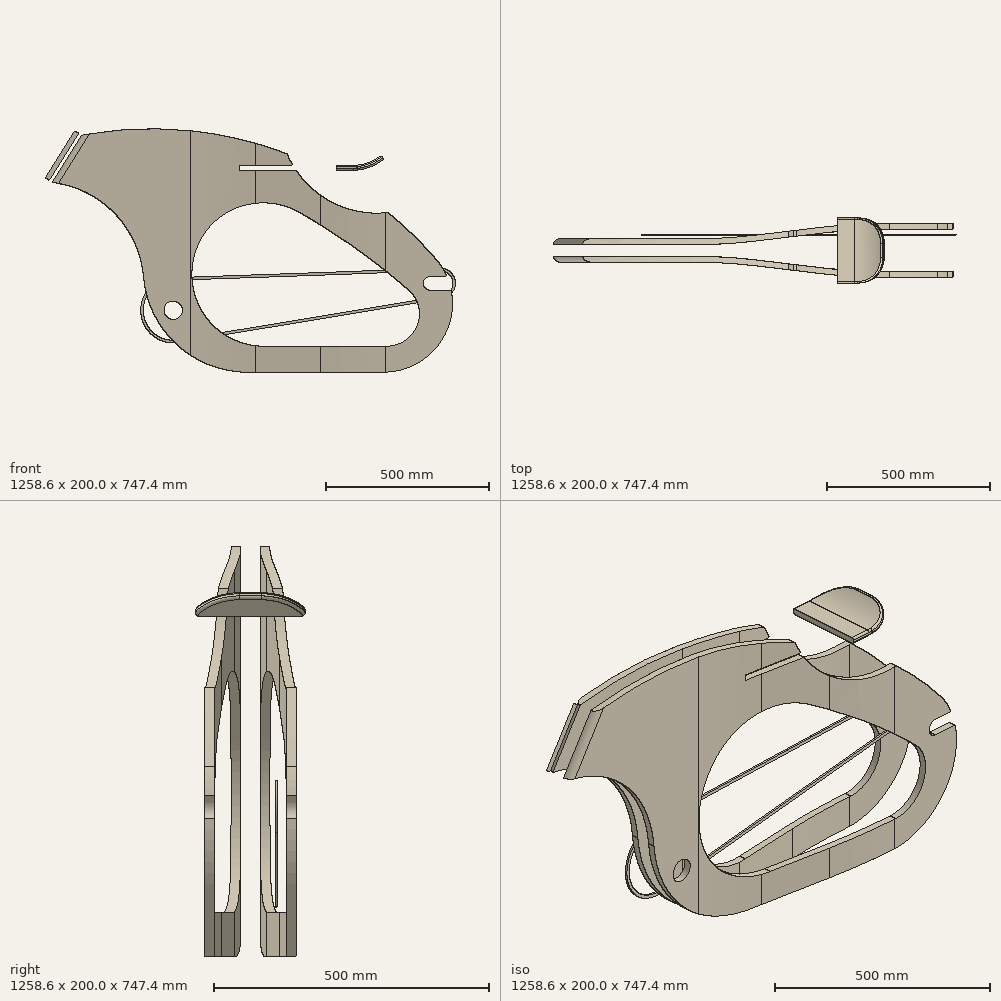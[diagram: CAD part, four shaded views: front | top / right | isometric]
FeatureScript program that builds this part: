
annotation { "Feature Type Name" : "Feature", "Feature Type Description" : "" }
export const myFeature = defineFeature(function(context is Context, id is Id, definition is map)
    precondition{}
    {
        {
            var Q0;
            Q0=qCreatedBy(makeId("Front.planeOp"),FACE);
            var sketch = newSketch(context, id + "F0", { "sketchPlane" : qUnion([Q0])});
            skCircle(sketch, "E0", {"center": v(766, 332.5) * mm, "radius": 332.5 * mm});
            skCircle(sketch, "E1", {"center": v(766, 332.5) * mm, "radius": 287.5 * mm});
            skLineSegment(sketch, "E2", {"start": v(-655.9, 304.94) * mm, "end": v(-438.79, 652.4) * mm});
            skCircle(sketch, "E3.0", {"center": v(766, 332.5) * mm, "radius": 269.5 * mm});
            skLineSegment(sketch, "E4", {"start": v(-438.79, 652.4) * mm, "end": v(-348.7, 796.57) * mm});
            skLineSegment(sketch, "E5", {"start": v(-700, 332.5) * mm, "end": v(-655.9, 304.94) * mm});
            skLineSegment(sketch, "E6.rect.bottom", {"start": v(-423.52, 642.86) * mm, "end": v(-454.05, 661.94) * mm});
            skLineSegment(sketch, "E6.rect.top", {"start": v(-333.44, 787.03) * mm, "end": v(-363.97, 806.1) * mm});
            skLineSegment(sketch, "E6.rect.right", {"start": v(-454.05, 661.94) * mm, "end": v(-363.97, 806.1) * mm});
            skPoint(sketch, "E6.rect.middle", {"position": v(-393.74, 724.48) * mm});
            skLineSegment(sketch, "E7", {"start": v(-333.44, 787.03) * mm, "end": v(-423.52, 642.86) * mm});
            skCircle(sketch, "E8", {"center": v(766, 332.5) * mm, "radius": 6 * mm, "construction": true});
            skLineSegment(sketch, "E9", {"start": v(736, 338.5) * mm, "end": v(796, 338.5) * mm, "construction": true});
            skLineSegment(sketch, "E10", {"start": v(736, 326.5) * mm, "end": v(796, 326.5) * mm, "construction": true});
            skArc(sketch, "E11", {"start": v(736, 338.5) * mm, "mid": v(730, 332.5) * mm, "end": v(736, 326.5) * mm, "construction": true});
            skLineSegment(sketch, "E12.bottom", {"start": v(796, 358.5) * mm, "end": v(711, 358.5) * mm, "construction": true});
            skLineSegment(sketch, "E12.top", {"start": v(796, 306.5) * mm, "end": v(711, 306.5) * mm, "construction": true});
            skLineSegment(sketch, "E12.left", {"start": v(796, 358.5) * mm, "end": v(796, 338.5) * mm, "construction": true});
            skLineSegment(sketch, "E12.right", {"start": v(711, 358.5) * mm, "end": v(711, 306.5) * mm, "construction": true});
            skLineSegment(sketch, "E13.trimOffspring", {"start": v(796, 326.5) * mm, "end": v(796, 306.5) * mm, "construction": true});
            skCircle(sketch, "E14", {"center": v(-700, 332.5) * mm, "radius": 332.5 * mm});
            skSolve(sketch);
        }
        {
            var Q0;
            Q0=qCreatedBy(makeId("Front.planeOp"),FACE);
            var sketch = newSketch(context, id + "F1", { "sketchPlane" : qUnion([Q0])});
            skCircle(sketch, "E15", {"center": v(-52.74, 250) * mm, "radius": 28 * mm});
            skPoint(sketch, "E16.rect.middle", {"position": v(-393.74, 724.48) * mm});
            skCircle(sketch, "E17", {"center": v(-52.74, 250) * mm, "radius": 220 * mm, "construction": true});
            skLineSegment(sketch, "E18", {"start": v(-333.44, 787.03) * mm, "end": v(-423.52, 642.86) * mm});
            skCircle(sketch, "E19", {"center": v(766.48, 332.5) * mm, "radius": 6 * mm, "construction": true});
            skArc(sketch, "E20", {"start": v(499.62, 680) * mm, "mid": v(549.62, 688.58) * mm, "end": v(593.9, 713.33) * mm});
            skLineSegment(sketch, "E21", {"start": v(499.62, 680) * mm, "end": v(149.62, 680) * mm});
            skArc(sketch, "E22", {"start": v(-144.1, 352.65) * mm, "mid": v(-41.65, 144.25) * mm, "end": v(174.74, 60) * mm});
            skArc(sketch, "E23", {"start": v(-144.1, 352.65) * mm, "mid": v(-232.4, 547.25) * mm, "end": v(-423.52, 642.86) * mm});
            skArc(sketch, "E24", {"start": v(786.48, 60) * mm, "mid": v(881.52, 114.61) * mm, "end": v(882.18, 224.23) * mm, "construction": true});
            skLineSegment(sketch, "E25", {"start": v(174.74, 60) * mm, "end": v(786.48, 60) * mm});
            skLineSegment(sketch, "E26", {"start": v(896.48, 395.04) * mm, "end": v(896.48, -82) * mm, "construction": true});
            skLineSegment(sketch, "E27", {"start": v(858.4, 311.5) * mm, "end": v(736, 311.5) * mm});
            skArc(sketch, "E28", {"start": v(736, 311.5) * mm, "mid": v(715, 332.5) * mm, "end": v(736, 353.5) * mm});
            skLineSegment(sketch, "E29", {"start": v(736, 353.5) * mm, "end": v(830.06, 353.5) * mm});
            skArc(sketch, "E30", {"start": v(296.56, 729.92) * mm, "mid": v(421.78, 588.55) * mm, "end": v(606.66, 550) * mm});
            skArc(sketch, "E31.trimOffspring", {"start": v(296.56, 729.92) * mm, "mid": v(-14.43, 802.69) * mm, "end": v(-333.44, 787.03) * mm});
            skArc(sketch, "E32", {"start": v(882.18, 224.23) * mm, "mid": v(633.17, 527.8) * mm, "end": v(296.56, 729.92) * mm, "construction": true});
            skArc(sketch, "E33", {"start": v(882.18, 224.23) * mm, "mid": v(759.66, 400) * mm, "end": v(606.66, 550) * mm});
            skArc(sketch, "E34", {"start": v(594.53, 60) * mm, "mid": v(785.37, 182.37) * mm, "end": v(753.8, 406.86) * mm});
            skSolve(sketch);
        }
        {
            var Q0;
            Q0=qCreatedBy(makeId("Front.planeOp"),FACE);
            var sketch = newSketch(context, id + "F2", { "sketchPlane" : qUnion([Q0])});
            skArc(sketch, "E35.4", {"start": v(332.47, 551.53) * mm, "mid": v(11.46, 415.97) * mm, "end": v(224.22, 140) * mm});
            skLineSegment(sketch, "E35.5", {"start": v(224.22, 140) * mm, "end": v(726.48, 140) * mm});
            skArc(sketch, "E36", {"start": v(726.48, 140) * mm, "mid": v(772.68, 170.88) * mm, "end": v(761.81, 225.37) * mm, "construction": true});
            skArc(sketch, "E37", {"start": v(761.81, 225.37) * mm, "mid": v(558.18, 402.98) * mm, "end": v(332.47, 551.53) * mm});
            skLineSegment(sketch, "E38", {"start": v(827.43, 311.5) * mm, "end": v(736, 311.5) * mm});
            skLineSegment(sketch, "E39", {"start": v(736, 353.5) * mm, "end": v(796.96, 353.5) * mm});
            skArc(sketch, "E40", {"start": v(736, 311.5) * mm, "mid": v(715, 332.5) * mm, "end": v(736, 353.5) * mm});
            skArc(sketch, "E41", {"start": v(796.96, 353.5) * mm, "mid": v(822.9, 340.27) * mm, "end": v(827.43, 311.5) * mm});
            skArc(sketch, "E42", {"start": v(604.53, 140) * mm, "mid": v(696.45, 203.56) * mm, "end": v(669.42, 312) * mm});
            skSolve(sketch);
        }
        {
            var Q0;
            Q0=sQuery(id+"F0.wireOp",VERTEX,"E2.end");
            var Q1;
            Q1=sQuery(id+"F0.wireOp",EDGE,"E2");
            cPlane(context, id + "F3", {"entities" : qUnion([Q0, Q1]), "cplaneType" : CPlaneType.CURVE_POINT, "offset" : 150 * mm, "width" : 150 * mm, "height" : 150 * mm});
        }
        {
            var Q0;
            Q0=qCreatedBy(id+"F3.planeOp",FACE);
            var sketch = newSketch(context, id + "F4", { "sketchPlane" : qUnion([Q0])});
            skCircle(sketch, "E43", {"center": v(-717.83, 0) * mm, "radius": 19 * mm});
            skSolve(sketch);
        }
        {
            var Q0;
            Q0=makeQuery(id+"F4.imprint","IMPRINT",FACE,{"disambiguationData":[TD([[makeQuery(id+"F4.imprint","IMPRINT",EDGE,{"derivedFrom":sQuery(id+"F4.wireOp",EDGE,"E43")}),1.0]])]});
            extrude(context, id + "F5", {"entities" : qUnion([Q0]), "depth" : 170 * mm});
        }
        {
            var Q0;
            Q0=makeQuery(id+"F5.opExtrude","CAP_FACE",FACE,{"disambiguationData":[OSD([sQuery(id+"F4.wireOp",EDGE,"E43")])],"isStart":false});
            var Q1;
            Q1=makeQuery(id+"F5.opExtrude","CAP_FACE",FACE,{"disambiguationData":[OSD([sQuery(id+"F4.wireOp",EDGE,"E43")])],"isStart":true});
            shell(context, id + "F6", {"entities" : qUnion([Q0, Q1]), "thickness" : 2 * mm});
        }
        {
            var Q0;
            Q0=sQuery(id+"F0.wireOp",EDGE,"E2");
            cPlane(context, id + "F7", {"entities" : qUnion([Q0]), "cplaneType" : CPlaneType.LINE_ANGLE, "offset" : 150 * mm, "angle" : 0 * degree, "width" : 150 * mm, "height" : 150 * mm});
        }
        {
            var Q0;
            Q0=qCreatedBy(id+"F7.planeOp",FACE);
            var sketch = newSketch(context, id + "F8", { "sketchPlane" : qUnion([Q0])});
            skLineSegment(sketch, "E44", {"start": v(0, 181.22) * mm, "end": v(0, -136.17) * mm, "construction": true});
            skLineSegment(sketch, "E45", {"start": v(-70, -99.25) * mm, "end": v(-70, 210.75) * mm});
            skArc(sketch, "E46", {"start": v(-70, 210.75) * mm, "mid": v(0, 280.75) * mm, "end": v(70, 210.75) * mm});
            skLineSegment(sketch, "E47", {"start": v(70, 210.75) * mm, "end": v(70, -99.25) * mm});
            skLineSegment(sketch, "E48", {"start": v(0, 280.75) * mm, "end": v(0, 606.14) * mm});
            skSolve(sketch);
        }
        {
            var Q0;
            Q0=sQuery(id+"F8.wireOp",VERTEX,"E45.start");
            var Q1;
            Q1=sQuery(id+"F8.wireOp",EDGE,"E45");
            cPlane(context, id + "F9", {"entities" : qUnion([Q0, Q1]), "cplaneType" : CPlaneType.CURVE_POINT, "offset" : 150 * mm, "width" : 150 * mm, "height" : 150 * mm});
        }
        {
            var Q0;
            Q0=qCreatedBy(id+"F9.planeOp",FACE);
            var sketch = newSketch(context, id + "F10", { "sketchPlane" : qUnion([Q0])});
            skCircle(sketch, "E49", {"center": v(-717.83, -70) * mm, "radius": 14.29 * mm});
            skSolve(sketch);
        }
        {
            var Q0;
            Q0=makeQuery(id+"F10.imprint","IMPRINT",FACE,{"disambiguationData":[TD([[makeQuery(id+"F10.imprint","IMPRINT",EDGE,{"derivedFrom":sQuery(id+"F10.wireOp",EDGE,"E49")}),1.0]])]});
            var Q1;
            Q1=sQuery(id+"F10.wireOp",EDGE,"E49");
            var Q2;
            Q2=sQuery(id+"F8.wireOp",EDGE,"E45");
            var Q3;
            Q3=sQuery(id+"F8.wireOp",EDGE,"E46");
            var Q4;
            Q4=sQuery(id+"F8.wireOp",EDGE,"E47");
            sweep(context, id + "F11", {"profiles" : qUnion([Q0]), "surfaceProfiles" : qUnion([Q1]), "path" : qUnion([Q2, Q3, Q4])});
        }
        {
            var Q0;
            Q0=sQuery(id+"F8.wireOp",EDGE,"E48");
            var Q1;
            Q1=sQuery(id+"F8.wireOp",VERTEX,"E48.start");
            cPlane(context, id + "F12", {"entities" : qUnion([Q0, Q1]), "cplaneType" : CPlaneType.CURVE_POINT, "offset" : 150 * mm, "width" : 150 * mm, "height" : 150 * mm});
        }
        {
            var Q0;
            Q0=qCreatedBy(id+"F12.planeOp",FACE);
            var sketch = newSketch(context, id + "F13", { "sketchPlane" : qUnion([Q0])});
            skCircle(sketch, "E50", {"center": v(-717.83, 0) * mm, "radius": 14.29 * mm});
            skSolve(sketch);
        }
        {
            var Q0;
            Q0=makeQuery(id+"F13.imprint","IMPRINT",FACE,{"disambiguationData":[TD([[makeQuery(id+"F13.imprint","IMPRINT",EDGE,{"derivedFrom":sQuery(id+"F13.wireOp",EDGE,"E50")}),1.0]])]});
            extrude(context, id + "F14", {"entities" : qUnion([Q0]), "operationType" : NewBodyOperationType.ADD, "depth" : 250 * mm});
        }
        {
            var Q0;
            Q0=makeQuery(id+"F11.opSweep","CAP_FACE",FACE,{"disambiguationData":[OSD([sQuery(id+"F8.wireOp",VERTEX,"E45.start"),sQuery(id+"F10.wireOp",EDGE,"E49")])],"isStart":true});
            var Q1;
            Q1=makeQuery(id+"F11.opSweep","CAP_FACE",FACE,{"disambiguationData":[OSD([sQuery(id+"F8.wireOp",VERTEX,"E47.end"),sQuery(id+"F10.wireOp",EDGE,"E49")])],"isStart":false});
            var Q2;
            Q2=makeQuery(id+"F14.opExtrude","CAP_FACE",FACE,{"disambiguationData":[OSD([sQuery(id+"F13.wireOp",EDGE,"E50")])],"isStart":false});
            shell(context, id + "F15", {"entities" : qUnion([Q0, Q1, Q2]), "thickness" : 2 * mm});
        }
        {
            var Q0;
            Q0=qCreatedBy(makeId("Top.planeOp"),FACE);
            var sketch = newSketch(context, id + "F16", { "sketchPlane" : qUnion([Q0])});
            skLineSegment(sketch, "E51", {"start": v(1100, 65) * mm, "end": v(600, 65) * mm});
            skLineSegment(sketch, "E52", {"start": v(-998.59, 17.5) * mm, "end": v(1.41, 17.5) * mm});
            skArc(sketch, "E53", {"start": v(1.41, 17.5) * mm, "mid": v(101.59, 20.48) * mm, "end": v(201.41, 29.4) * mm});
            skArc(sketch, "E54", {"start": v(600, 65) * mm, "mid": v(499.82, 62.02) * mm, "end": v(400, 53.1) * mm});
            skLineSegment(sketch, "E55", {"start": v(201.41, 29.4) * mm, "end": v(400, 53.1) * mm});
            skLineSegment(sketch, "E56.0", {"start": v(1100, 83) * mm, "end": v(600, 83) * mm});
            skArc(sketch, "E56.1", {"start": v(600, 83) * mm, "mid": v(498.75, 80) * mm, "end": v(397.87, 70.98) * mm});
            skLineSegment(sketch, "E56.2", {"start": v(199.28, 47.27) * mm, "end": v(397.87, 70.98) * mm});
            skArc(sketch, "E56.3", {"start": v(1.41, 35.5) * mm, "mid": v(100.52, 38.44) * mm, "end": v(199.28, 47.27) * mm});
            skLineSegment(sketch, "E56.4", {"start": v(-998.59, 35.5) * mm, "end": v(1.41, 35.5) * mm});
            skLineSegment(sketch, "E57", {"start": v(1100, 65) * mm, "end": v(1100, 83) * mm});
            skLineSegment(sketch, "E58", {"start": v(-998.59, 17.5) * mm, "end": v(-998.59, 35.5) * mm});
            skSolve(sketch);
        }
        {
            var Q0;
            Q0=makeQuery(id+"F1.imprint","IMPRINT",FACE,{"disambiguationData":[TD([[makeQuery(id+"F1.imprint","IMPRINT",EDGE,{"derivedFrom":sQuery(id+"F1.wireOp",EDGE,"E15")}),-1.0]])]});
            extrude(context, id + "F17", {"entities" : qUnion([Q0]), "oppositeDirection" : true, "depth" : 150 * mm});
        }
        {
            var Q0;
            Q0=makeQuery(id+"F2.imprint","IMPRINT",FACE,{"disambiguationData":[TD([[makeQuery(id+"F2.imprint","IMPRINT",EDGE,{"derivedFrom":sQuery(id+"F2.wireOp",EDGE,"E35.4")}),1.0]])]});
            var Q1;
            Q1=makeQuery(id+"F2.imprint","IMPRINT",FACE,{"disambiguationData":[TD([[makeQuery(id+"F2.imprint","IMPRINT",EDGE,{"derivedFrom":sQuery(id+"F2.wireOp",EDGE,"E38")}),-1.0]])]});
            extrude(context, id + "F18", {"entities" : qUnion([Q0, Q1]), "operationType" : NewBodyOperationType.REMOVE, "oppositeDirection" : true, "depth" : 200 * mm});
        }
        {
            var Q0;
            Q0=qCreatedBy(makeId("Front.planeOp"),FACE);
            var sketch = newSketch(context, id + "F19", { "sketchPlane" : qUnion([Q0])});
            skLineSegment(sketch, "E59", {"start": v(499.62, 680) * mm, "end": v(149.62, 680) * mm});
            skArc(sketch, "E60", {"start": v(499.62, 680) * mm, "mid": v(549.62, 688.58) * mm, "end": v(593.9, 713.33) * mm});
            skArc(sketch, "E61.0", {"start": v(499.62, 695) * mm, "mid": v(544.62, 702.72) * mm, "end": v(584.47, 725) * mm});
            skLineSegment(sketch, "E61.1", {"start": v(499.62, 695) * mm, "end": v(149.62, 695) * mm});
            skLineSegment(sketch, "E62", {"start": v(593.9, 713.33) * mm, "end": v(584.47, 725) * mm});
            skLineSegment(sketch, "E63", {"start": v(149.62, 680) * mm, "end": v(149.62, 695) * mm});
            skSolve(sketch);
        }
        {
            var Q0;
            Q0=makeQuery(id+"F16.imprint","IMPRINT",FACE,{"disambiguationData":[TD([[makeQuery(id+"F16.imprint","IMPRINT",EDGE,{"derivedFrom":sQuery(id+"F16.wireOp",EDGE,"E51")}),-1.0]])]});
            extrude(context, id + "F20", {"entities" : qUnion([Q0]), "operationType" : NewBodyOperationType.INTERSECT, "depth" : 1000 * mm});
        }
        {
            var Q0;
            Q0=makeQuery(id+"F17.opExtrude","SWEPT_BODY",BODY,{"disambiguationData":[OSD([sQuery(id+"F1.wireOp",EDGE,"E15"),sQuery(id+"F1.wireOp",EDGE,"E18"),sQuery(id+"F1.wireOp",EDGE,"f25a1a5c-b35a-4eaa-8e16-6169ae110cd0"),sQuery(id+"F1.wireOp",EDGE,"56185d79-83a2-4922-81b8-f2a27202fd78"),sQuery(id+"F1.wireOp",EDGE,"c2120ab2-a2c6-4db6-bdfa-dd0143dbe7f6"),sQuery(id+"F1.wireOp",EDGE,"d6b472ae-8588-43ed-990c-50ee3ed74349"),sQuery(id+"F1.wireOp",EDGE,"64d2bcdb-48c4-4ea9-94b1-3d4cdc629e19"),sQuery(id+"F1.wireOp",EDGE,"7d159a81-d20a-4d29-8569-c734789b89ba.0"),sQuery(id+"F1.wireOp",EDGE,"7d159a81-d20a-4d29-8569-c734789b89ba.1"),sQuery(id+"F1.wireOp",EDGE,"7d159a81-d20a-4d29-8569-c734789b89ba.2"),sQuery(id+"F1.wireOp",EDGE,"fa78dc51-c197-49c6-b8ef-f44956650a6e"),sQuery(id+"F1.wireOp",EDGE,"1d27aa24-91d2-4d14-8a43-1a7035f57801"),sQuery(id+"F1.wireOp",EDGE,"E22"),sQuery(id+"F1.wireOp",EDGE,"b122f575-9e76-4623-8be3-a576d456f2d0"),sQuery(id+"F1.wireOp",EDGE,"E23")])]});
            var Q1;
            Q1=qCreatedBy(makeId("Front.planeOp"),FACE);
            mirror(context, id + "F21", {"entities" : qUnion([Q0]), "mirrorPlane" : qUnion([Q1])});
        }
        {
            var Q0;
            Q0=makeQuery(id+"F19.imprint","IMPRINT",FACE,{"disambiguationData":[TD([[makeQuery(id+"F19.imprint","IMPRINT",EDGE,{"derivedFrom":sQuery(id+"F19.wireOp",EDGE,"E59")}),-1.0]])]});
            extrude(context, id + "F22", {"entities" : qUnion([Q0]), "endBound" : BoundingType.SYMMETRIC, "depth" : 200 * mm});
        }
        {
            var Q0;
            Q0=makeQuery(id+"F22.opExtrude","CAP_EDGE",EDGE,{"disambiguationData":[OSD([sQuery(id+"F19.wireOp",EDGE,"E62")])],"isStart":false});
            var Q1;
            Q1=makeQuery(id+"F22.opExtrude","CAP_EDGE",EDGE,{"disambiguationData":[OSD([sQuery(id+"F19.wireOp",EDGE,"E62")])],"isStart":true});
            fillet(context, id + "F23", {"entities" : qUnion([Q0, Q1]), "radius" : 80 * mm, "tangentPropagation" : true, "allowEdgeOverflow" : false});
        }
        {
            var Q0;
            Q0=makeQuery(id+"F22.opExtrude","CAP_EDGE",EDGE,{"disambiguationData":[OSD([sQuery(id+"F19.wireOp",EDGE,"E63")])],"isStart":false});
            chamfer(context, id + "F24", {"entities" : qUnion([Q0]), "chamferType" : ChamferType.TWO_OFFSETS, "width1" : 30 * mm, "oppositeDirection" : false, "width2" : 200 * mm});
        }
        {
            var Q0;
            Q0=makeQuery(id+"F22.opExtrude","CAP_EDGE",EDGE,{"disambiguationData":[OSD([sQuery(id+"F19.wireOp",EDGE,"E63")])],"isStart":true});
            chamfer(context, id + "F25", {"entities" : qUnion([Q0]), "chamferType" : ChamferType.TWO_OFFSETS, "width1" : 200 * mm, "oppositeDirection" : false, "width2" : 30 * mm, "tangentPropagation" : true});
        }
        {
            var Q0;
            {var subQ0=sQuery(id+"F19.wireOp",EDGE,"E63");Q0=makeQuery(id+"F24.opChamfer","BLEND_EDGE",EDGE,{"blendedFrom":[makeQuery(id+"F22.opExtrude","CAP_EDGE",EDGE,{"disambiguationData":[OSD([subQ0])],"isStart":false}),makeQuery(id+"F22.opExtrude","CAP_FACE",FACE,{"disambiguationData":[OSD([sQuery(id+"F19.wireOp",EDGE,"E59"),sQuery(id+"F19.wireOp",EDGE,"E60"),sQuery(id+"F19.wireOp",EDGE,"E61.0"),sQuery(id+"F19.wireOp",EDGE,"E61.1"),sQuery(id+"F19.wireOp",EDGE,"E62"),subQ0])],"isStart":false})],"blendedInto":[makeQuery(id+"F22.opExtrude","CAP_FACE",FACE,{"disambiguationData":[OSD([sQuery(id+"F19.wireOp",EDGE,"E59"),sQuery(id+"F19.wireOp",EDGE,"E60"),sQuery(id+"F19.wireOp",EDGE,"E61.0"),sQuery(id+"F19.wireOp",EDGE,"E61.1"),sQuery(id+"F19.wireOp",EDGE,"E62"),subQ0])],"isStart":false})]});}
            var Q1;
            {var subQ0=sQuery(id+"F19.wireOp",EDGE,"E63");Q1=makeQuery(id+"F25.opChamfer","BLEND_EDGE",EDGE,{"blendedFrom":[makeQuery(id+"F22.opExtrude","CAP_EDGE",EDGE,{"disambiguationData":[OSD([subQ0])],"isStart":true}),makeQuery(id+"F22.opExtrude","CAP_FACE",FACE,{"disambiguationData":[OSD([sQuery(id+"F19.wireOp",EDGE,"E59"),sQuery(id+"F19.wireOp",EDGE,"E60"),sQuery(id+"F19.wireOp",EDGE,"E61.0"),sQuery(id+"F19.wireOp",EDGE,"E61.1"),sQuery(id+"F19.wireOp",EDGE,"E62"),subQ0])],"isStart":true})],"blendedInto":[makeQuery(id+"F22.opExtrude","CAP_FACE",FACE,{"disambiguationData":[OSD([sQuery(id+"F19.wireOp",EDGE,"E59"),sQuery(id+"F19.wireOp",EDGE,"E60"),sQuery(id+"F19.wireOp",EDGE,"E61.0"),sQuery(id+"F19.wireOp",EDGE,"E61.1"),sQuery(id+"F19.wireOp",EDGE,"E62"),subQ0])],"isStart":true})]});}
            fillet(context, id + "F26", {"entities" : qUnion([Q0, Q1]), "radius" : 300 * mm, "tangentPropagation" : true, "allowEdgeOverflow" : false});
        }
        {
            var Q0;
            {var subQ0=sQuery(id+"F19.wireOp",EDGE,"E63");Q0=makeQuery(id+"F25.opChamfer","BLEND_EDGE",EDGE,{"blendedFrom":[makeQuery(id+"F22.opExtrude","CAP_EDGE",EDGE,{"disambiguationData":[OSD([subQ0])],"isStart":true}),makeQuery(id+"F22.boolean.opBoolean","SPLIT",FACE,{"disambiguationData":[TD([makeQuery(id+"F21.opPattern","COPY",FACE,{"derivedFrom":makeQuery(id+"F20.boolean.opBoolean","COPY",FACE,{"derivedFrom":makeQuery(id+"F20.opExtrude","SWEPT_FACE",FACE,{"disambiguationData":[OSD([sQuery(id+"F16.wireOp",EDGE,"E53")])]})}),"instanceName":"1"})])],"derivedFrom":makeQuery(id+"F22.opExtrude","SWEPT_FACE",FACE,{"disambiguationData":[OSD([subQ0])]})})],"blendedInto":[makeQuery(id+"F22.boolean.opBoolean","SPLIT",FACE,{"disambiguationData":[TD([makeQuery(id+"F21.opPattern","COPY",FACE,{"derivedFrom":makeQuery(id+"F20.boolean.opBoolean","COPY",FACE,{"derivedFrom":makeQuery(id+"F20.opExtrude","SWEPT_FACE",FACE,{"disambiguationData":[OSD([sQuery(id+"F16.wireOp",EDGE,"E53")])]})}),"instanceName":"1"})])],"derivedFrom":makeQuery(id+"F22.opExtrude","SWEPT_FACE",FACE,{"disambiguationData":[OSD([subQ0])]})})]});}
            var Q1;
            {var subQ0=sQuery(id+"F19.wireOp",EDGE,"E63");Q1=makeQuery(id+"F24.opChamfer","BLEND_EDGE",EDGE,{"blendedFrom":[makeQuery(id+"F22.opExtrude","CAP_EDGE",EDGE,{"disambiguationData":[OSD([subQ0])],"isStart":false}),makeQuery(id+"F22.boolean.opBoolean","SPLIT",FACE,{"disambiguationData":[TD([makeQuery(id+"F21.opPattern","COPY",FACE,{"derivedFrom":makeQuery(id+"F20.boolean.opBoolean","COPY",FACE,{"derivedFrom":makeQuery(id+"F20.opExtrude","SWEPT_FACE",FACE,{"disambiguationData":[OSD([sQuery(id+"F16.wireOp",EDGE,"E56.3")])]})}),"instanceName":"1"})])],"derivedFrom":makeQuery(id+"F22.opExtrude","SWEPT_FACE",FACE,{"disambiguationData":[OSD([subQ0])]})})],"blendedInto":[makeQuery(id+"F22.boolean.opBoolean","SPLIT",FACE,{"disambiguationData":[TD([makeQuery(id+"F21.opPattern","COPY",FACE,{"derivedFrom":makeQuery(id+"F20.boolean.opBoolean","COPY",FACE,{"derivedFrom":makeQuery(id+"F20.opExtrude","SWEPT_FACE",FACE,{"disambiguationData":[OSD([sQuery(id+"F16.wireOp",EDGE,"E56.3")])]})}),"instanceName":"1"})])],"derivedFrom":makeQuery(id+"F22.opExtrude","SWEPT_FACE",FACE,{"disambiguationData":[OSD([subQ0])]})})]});}
            fillet(context, id + "F27", {"entities" : qUnion([Q0, Q1]), "radius" : 15 * mm, "tangentPropagation" : true, "allowEdgeOverflow" : false});
        }
        {
            var Q0;
            {var subQ0=sQuery(id+"F19.wireOp",EDGE,"E63");var subQ1=sQuery(id+"F19.wireOp",EDGE,"E61.1");var subQ2=makeQuery(id+"F22.opExtrude","SWEPT_FACE",FACE,{"disambiguationData":[OSD([subQ1])]});Q0=makeQuery(id+"F27.opFillet","BLEND_EDGE",EDGE,{"blendedFrom":[makeQuery(id+"F24.opChamfer","BLEND_EDGE",EDGE,{"blendedFrom":[makeQuery(id+"F22.opExtrude","CAP_EDGE",EDGE,{"disambiguationData":[OSD([subQ0])],"isStart":false}),makeQuery(id+"F22.boolean.opBoolean","SPLIT",FACE,{"disambiguationData":[TD([makeQuery(id+"F21.opPattern","COPY",FACE,{"derivedFrom":makeQuery(id+"F20.boolean.opBoolean","COPY",FACE,{"derivedFrom":makeQuery(id+"F20.opExtrude","SWEPT_FACE",FACE,{"disambiguationData":[OSD([sQuery(id+"F16.wireOp",EDGE,"E56.3")])]})}),"instanceName":"1"})])],"derivedFrom":makeQuery(id+"F22.opExtrude","SWEPT_FACE",FACE,{"disambiguationData":[OSD([subQ0])]})})],"blendedInto":[makeQuery(id+"F22.boolean.opBoolean","SPLIT",FACE,{"disambiguationData":[TD([makeQuery(id+"F21.opPattern","COPY",FACE,{"derivedFrom":makeQuery(id+"F20.boolean.opBoolean","COPY",FACE,{"derivedFrom":makeQuery(id+"F20.opExtrude","SWEPT_FACE",FACE,{"disambiguationData":[OSD([sQuery(id+"F16.wireOp",EDGE,"E56.3")])]})}),"instanceName":"1"})])],"derivedFrom":makeQuery(id+"F22.opExtrude","SWEPT_FACE",FACE,{"disambiguationData":[OSD([subQ0])]})})]}),subQ2],"blendedInto":[subQ2]});}
            var Q1;
            {var subQ0=sQuery(id+"F19.wireOp",EDGE,"E63");var subQ2=sQuery(id+"F19.wireOp",EDGE,"E59");var subQ3=makeQuery(id+"F22.opExtrude","SWEPT_FACE",FACE,{"disambiguationData":[OSD([subQ2])]});Q1=makeQuery(id+"F27.opFillet","BLEND_EDGE",EDGE,{"blendedFrom":[makeQuery(id+"F24.opChamfer","BLEND_EDGE",EDGE,{"blendedFrom":[makeQuery(id+"F22.opExtrude","CAP_EDGE",EDGE,{"disambiguationData":[OSD([subQ0])],"isStart":false}),makeQuery(id+"F22.boolean.opBoolean","SPLIT",FACE,{"disambiguationData":[TD([makeQuery(id+"F21.opPattern","COPY",FACE,{"derivedFrom":makeQuery(id+"F20.boolean.opBoolean","COPY",FACE,{"derivedFrom":makeQuery(id+"F20.opExtrude","SWEPT_FACE",FACE,{"disambiguationData":[OSD([sQuery(id+"F16.wireOp",EDGE,"E56.3")])]})}),"instanceName":"1"})])],"derivedFrom":makeQuery(id+"F22.opExtrude","SWEPT_FACE",FACE,{"disambiguationData":[OSD([subQ0])]})})],"blendedInto":[makeQuery(id+"F22.boolean.opBoolean","SPLIT",FACE,{"disambiguationData":[TD([makeQuery(id+"F21.opPattern","COPY",FACE,{"derivedFrom":makeQuery(id+"F20.boolean.opBoolean","COPY",FACE,{"derivedFrom":makeQuery(id+"F20.opExtrude","SWEPT_FACE",FACE,{"disambiguationData":[OSD([sQuery(id+"F16.wireOp",EDGE,"E56.3")])]})}),"instanceName":"1"})])],"derivedFrom":makeQuery(id+"F22.opExtrude","SWEPT_FACE",FACE,{"disambiguationData":[OSD([subQ0])]})})]}),subQ3],"blendedInto":[subQ3]});}
            fillet(context, id + "F28", {"entities" : qUnion([Q0, Q1]), "radius" : 5 * mm, "tangentPropagation" : true, "allowEdgeOverflow" : false});
        }
        {
            var Q0;
            Q0=qCreatedBy(makeId("Front.planeOp"),FACE);
            cPlane(context, id + "F29", {"entities" : qUnion([Q0]), "cplaneType" : CPlaneType.OFFSET, "offset" : 45 * mm, "oppositeDirection" : true, "width" : 150 * mm, "height" : 150 * mm});
        }
        {
            var Q0;
            Q0=qCreatedBy(id+"F29.planeOp",FACE);
            var sketch = newSketch(context, id + "F30", { "sketchPlane" : qUnion([Q0])});
            skArc(sketch, "E64", {"start": v(-56.23, 349.94) * mm, "mid": v(-152.24, 240.06) * mm, "end": v(-36.38, 151.35) * mm});
            skArc(sketch, "E65", {"start": v(773.77, 285.64) * mm, "mid": v(813.26, 337.31) * mm, "end": v(764.16, 379.96) * mm});
            skLineSegment(sketch, "E66", {"start": v(764.16, 379.96) * mm, "end": v(454.4, 367.94) * mm});
            skLineSegment(sketch, "E67", {"start": v(-36.38, 151.35) * mm, "end": v(773.77, 285.64) * mm});
            skLineSegment(sketch, "E68.0", {"start": v(764.47, 371.97) * mm, "end": v(454.7, 359.94) * mm});
            skArc(sketch, "E68.1", {"start": v(772.46, 293.53) * mm, "mid": v(805.3, 336.5) * mm, "end": v(764.47, 371.97) * mm});
            skLineSegment(sketch, "E68.2", {"start": v(-37.7, 159.24) * mm, "end": v(772.46, 293.53) * mm});
            skArc(sketch, "E68.3", {"start": v(-55.95, 341.94) * mm, "mid": v(-144.28, 240.85) * mm, "end": v(-37.7, 159.24) * mm});
            skLineSegment(sketch, "E69", {"start": v(-56.23, 349.94) * mm, "end": v(377.9, 365.12) * mm});
            skArc(sketch, "E70", {"start": v(454.4, 367.94) * mm, "mid": v(416.15, 366.49) * mm, "end": v(377.9, 365.12) * mm});
            skLineSegment(sketch, "E71.0", {"start": v(-55.95, 341.94) * mm, "end": v(378.19, 357.12) * mm});
            skArc(sketch, "E71.1", {"start": v(454.7, 359.94) * mm, "mid": v(416.45, 358.5) * mm, "end": v(378.19, 357.12) * mm});
            skSolve(sketch);
        }
        {
            var Q0;
            Q0=makeQuery(id+"F30.imprint","IMPRINT",FACE,{"disambiguationData":[TD([[makeQuery(id+"F30.imprint","IMPRINT",EDGE,{"derivedFrom":sQuery(id+"F30.wireOp",EDGE,"E64")}),1.0]])]});
            extrude(context, id + "F31", {"entities" : qUnion([Q0]), "oppositeDirection" : true, "depth" : 5 * mm});
        }
        {
            var Q0;
            Q0=qCreatedBy(makeId("Front.planeOp"),FACE);
            var sketch = newSketch(context, id + "F32", { "sketchPlane" : qUnion([Q0])});
            skLineSegment(sketch, "E72", {"start": v(449.62, 695) * mm, "end": v(149.62, 695) * mm});
            skLineSegment(sketch, "E73", {"start": v(149.62, 695) * mm, "end": v(149.62, 680) * mm});
            skLineSegment(sketch, "E74", {"start": v(149.62, 680) * mm, "end": v(449.62, 680) * mm});
            skLineSegment(sketch, "E75", {"start": v(449.62, 680) * mm, "end": v(449.62, 695) * mm});
            skSolve(sketch);
        }
        {
            var Q0;
            Q0=makeQuery(id+"F32.imprint","IMPRINT",FACE,{"disambiguationData":[TD([[makeQuery(id+"F32.imprint","IMPRINT",EDGE,{"derivedFrom":sQuery(id+"F32.wireOp",EDGE,"E72")}),1.0]])]});
            extrude(context, id + "F33", {"entities" : qUnion([Q0]), "operationType" : NewBodyOperationType.REMOVE, "endBound" : BoundingType.SYMMETRIC, "oppositeDirection" : true, "depth" : 300 * mm});
        }
        {
            var Q0;
            Q0=makeQuery(id+"F21.opPattern","COPY",EDGE,{"derivedFrom":makeQuery(id+"F20.boolean.opBoolean","INTERSECT",EDGE,{"derivedFrom":[makeQuery(id+"F17.opExtrude","SWEPT_FACE",FACE,{"disambiguationData":[OSD([sQuery(id+"F1.wireOp",EDGE,"E18")])]}),makeQuery(id+"F20.opExtrude","SWEPT_FACE",FACE,{"disambiguationData":[OSD([sQuery(id+"F16.wireOp",EDGE,"E56.4")])]})]}),"instanceName":"1"});
            var Q1;
            Q1=makeQuery(id+"F20.boolean.opBoolean","INTERSECT",EDGE,{"derivedFrom":[makeQuery(id+"F17.opExtrude","SWEPT_FACE",FACE,{"disambiguationData":[OSD([sQuery(id+"F1.wireOp",EDGE,"E18")])]}),makeQuery(id+"F20.opExtrude","SWEPT_FACE",FACE,{"disambiguationData":[OSD([sQuery(id+"F16.wireOp",EDGE,"E56.4")])]})]});
            fillet(context, id + "F34", {"entities" : qUnion([Q0, Q1]), "radius" : 18 * mm, "tangentPropagation" : true, "allowEdgeOverflow" : false});
        }
        {
            var Q0;
            Q0=makeQuery(id+"F11.opSweep","SWEPT_BODY",BODY,{"disambiguationData":[OSD([sQuery(id+"F8.wireOp",EDGE,"E47"),sQuery(id+"F10.wireOp",EDGE,"E49")])]});
            deleteBodies(context, id + "F35", {"entities" : qUnion([Q0])});
        }
    });
